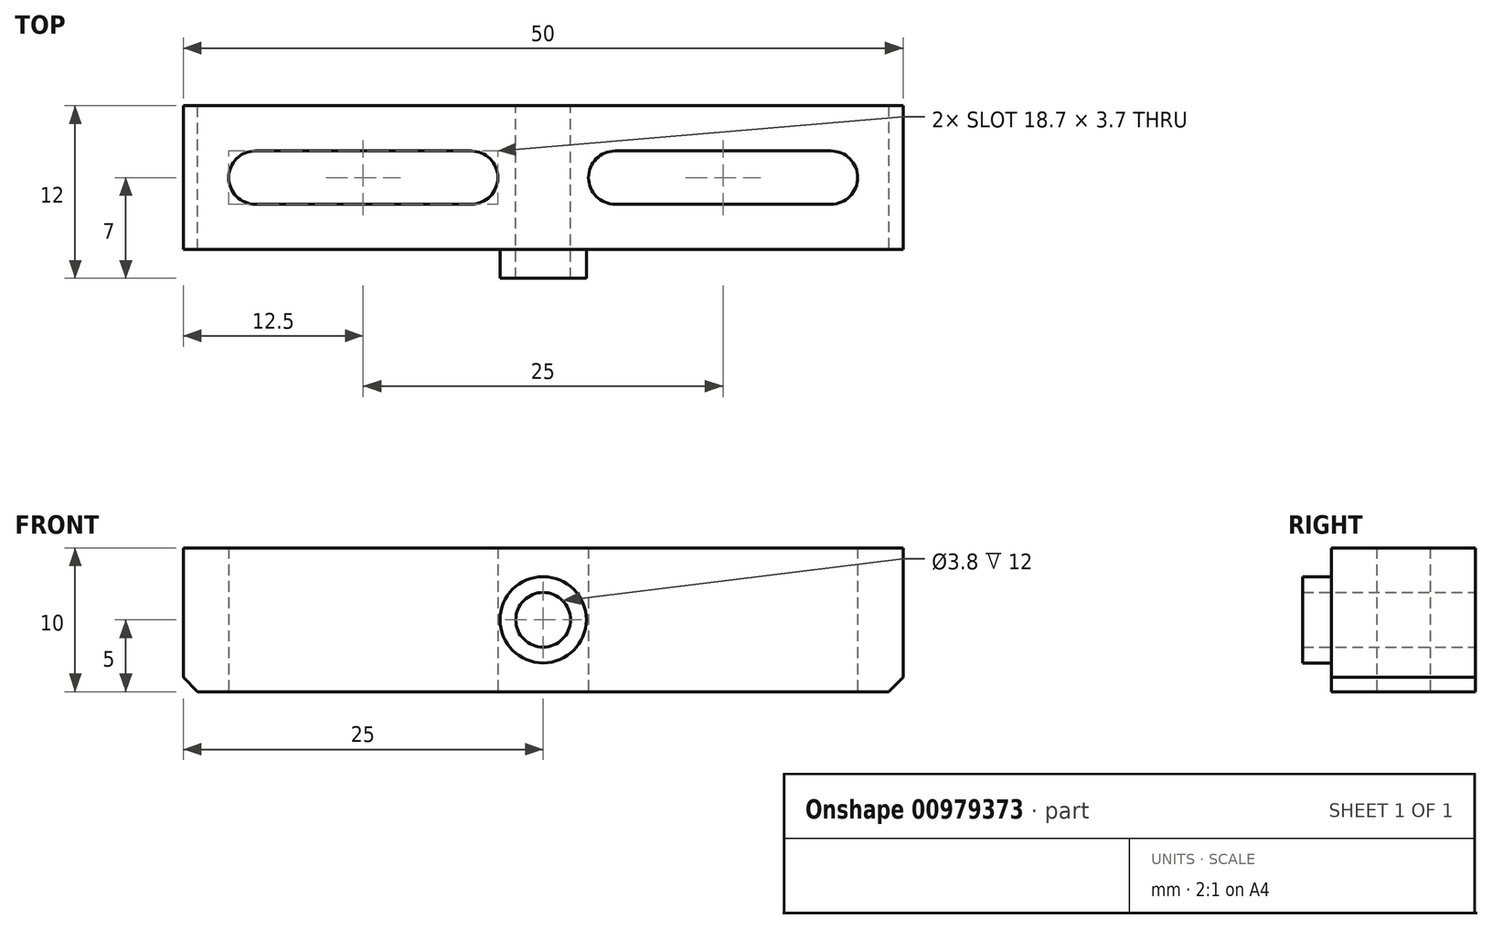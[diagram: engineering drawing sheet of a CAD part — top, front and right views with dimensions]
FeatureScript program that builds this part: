
annotation { "Feature Type Name" : "Feature", "Feature Type Description" : "" }
export const myFeature = defineFeature(function(context is Context, id is Id, definition is map)
    precondition{}
    {
        {
            var Q0;
            Q0=qCreatedBy(makeId("Front.planeOp"),FACE);
            var sketch = newSketch(context, id + "F0", { "sketchPlane" : qUnion([Q0])});
            skLineSegment(sketch, "E0.bottom", {"start": v(-25, 5) * mm, "end": v(25, 5) * mm});
            skLineSegment(sketch, "E0.top", {"start": v(-25, -5) * mm, "end": v(25, -5) * mm});
            skLineSegment(sketch, "E0.left", {"start": v(-25, 5) * mm, "end": v(-25, -5) * mm});
            skLineSegment(sketch, "E0.right", {"start": v(25, 5) * mm, "end": v(25, -5) * mm});
            skCircle(sketch, "E1", {"center": v(0, 0) * mm, "radius": 1.9 * mm});
            skSolve(sketch);
        }
        {
            var Q0;
            Q0=makeQuery(id+"F0.imprint","IMPRINT",FACE,{"disambiguationData":[TD([[makeQuery(id+"F0.imprint","IMPRINT",EDGE,{"derivedFrom":sQuery(id+"F0.wireOp",EDGE,"E0.top")}),1.0]])]});
            var Q1;
            Q1=makeQuery(id+"F0.imprint","IMPRINT",FACE,{"disambiguationData":[TD([[makeQuery(id+"F0.imprint","IMPRINT",EDGE,{"derivedFrom":sQuery(id+"F0.wireOp",EDGE,"WQmV3pCq-aRhs-lOnZ-NjPH-xWmHPh12bcor.bottom")}),-1.0]])]});
            var Q2;
            Q2=makeQuery(id+"F0.imprint","IMPRINT",FACE,{"disambiguationData":[TD([[makeQuery(id+"F0.imprint","IMPRINT",EDGE,{"derivedFrom":sQuery(id+"F0.wireOp",EDGE,"4fe1e560-5f00-40fb-89e2-31eaf53a3c980.MirrorCS")}),1.0]])]});
            var Q3;
            Q3=makeQuery(id+"F0.imprint","IMPRINT",FACE,{"disambiguationData":[TD([[makeQuery(id+"F0.imprint","IMPRINT",EDGE,{"derivedFrom":sQuery(id+"F0.wireOp",EDGE,"ZNvJAWPE-tP20-W4cz-rGWo-qfeXD5whcLuB")}),-1.0]])]});
            var Q4;
            Q4=makeQuery(id+"F0.imprint","IMPRINT",FACE,{"disambiguationData":[TD([[makeQuery(id+"F0.imprint","IMPRINT",EDGE,{"derivedFrom":sQuery(id+"F0.wireOp",EDGE,"E1")}),-1.0]])]});
            var Q5;
            Q5=makeQuery(id+"F0.imprint","IMPRINT",FACE,{"disambiguationData":[TD([[makeQuery(id+"F0.imprint","IMPRINT",EDGE,{"derivedFrom":sQuery(id+"F0.wireOp",EDGE,"fFYV0rMq-jki3-MS3X-DClv-uZveLAqEbOBl")}),1.0]])]});
            extrude(context, id + "F1", {"entities" : qUnion([Q0, Q1, Q2, Q3, Q4, Q5]), "endBound" : BoundingType.SYMMETRIC, "depth" : 10 * mm, "offsetDistance" : 25 * mm});
        }
        {
            var Q0;
            Q0=makeQuery(id+"F1.opExtrude","SWEPT_EDGE",EDGE,{"disambiguationData":[OSD([sQuery(id+"F0.wireOp",EDGE,"E0.top"),sQuery(id+"F0.wireOp",EDGE,"E0.left")])]});
            var Q1;
            Q1=makeQuery(id+"F1.opExtrude","SWEPT_EDGE",EDGE,{"disambiguationData":[OSD([sQuery(id+"F0.wireOp",EDGE,"E0.top"),sQuery(id+"F0.wireOp",EDGE,"E0.right")])]});
            chamfer(context, id + "F2", {"entities" : qUnion([Q0, Q1]), "width" : 1 * mm, "tangentPropagation" : true});
        }
        {
            var Q0;
            Q0=qCreatedBy(makeId("Top.planeOp"),FACE);
            var sketch = newSketch(context, id + "F3", { "sketchPlane" : qUnion([Q0])});
            skLineSegment(sketch, "E2", {"start": v(-20, 0) * mm, "end": v(-5, 0) * mm, "construction": true});
            skArc(sketch, "E3.0.startCap", {"start": v(-20, -1.85) * mm, "mid": v(-21.85, 0) * mm, "end": v(-20, 1.85) * mm});
            skArc(sketch, "E3.0.endCap", {"start": v(-5, 1.85) * mm, "mid": v(-3.15, 0) * mm, "end": v(-5, -1.85) * mm});
            skLineSegment(sketch, "E3.0.left", {"start": v(-20, 1.85) * mm, "end": v(-5, 1.85) * mm});
            skLineSegment(sketch, "E3.0.right", {"start": v(-20, -1.85) * mm, "end": v(-5, -1.85) * mm});
            skArc(sketch, "E4.MirrorCS", {"start": v(20, -1.85) * mm, "mid": v(21.85, 0) * mm, "end": v(20, 1.85) * mm});
            skLineSegment(sketch, "E5.MirrorCS", {"start": v(20, 0) * mm, "end": v(5, 0) * mm, "construction": true});
            skLineSegment(sketch, "E6.MirrorCS", {"start": v(20, 1.85) * mm, "end": v(5, 1.85) * mm});
            skLineSegment(sketch, "E7.MirrorCS", {"start": v(20, -1.85) * mm, "end": v(5, -1.85) * mm});
            skArc(sketch, "E8.MirrorCS", {"start": v(5, 1.85) * mm, "mid": v(3.15, 0) * mm, "end": v(5, -1.85) * mm});
            skSolve(sketch);
        }
        {
            var Q0;
            Q0 = qSketchRegion(id + "F3", true);
            extrude(context, id + "F4", {"entities" : qUnion([Q0]), "operationType" : NewBodyOperationType.REMOVE, "endBound" : BoundingType.SYMMETRIC, "depth" : 25 * mm, "offsetDistance" : 25 * mm});
        }
        {
            var Q0;
            Q0=makeQuery(id+"F1.opExtrude","CAP_FACE",FACE,{"disambiguationData":[OSD([sQuery(id+"F0.wireOp",EDGE,"E0.bottom"),sQuery(id+"F0.wireOp",EDGE,"E0.top"),sQuery(id+"F0.wireOp",EDGE,"E0.left"),sQuery(id+"F0.wireOp",EDGE,"E0.right"),sQuery(id+"F0.wireOp",EDGE,"E1")])],"isStart":false});
            var sketch = newSketch(context, id + "F5", { "sketchPlane" : qUnion([Q0])});
            skCircle(sketch, "E9", {"center": v(0, 0) * mm, "radius": 3 * mm});
            skSolve(sketch);
        }
        {
            var Q0;
            Q0=makeQuery(id+"F5.imprint","IMPRINT",FACE,{"disambiguationData":[TD([[makeQuery(id+"F5.imprint","IMPRINT",EDGE,{"derivedFrom":sQuery(id+"F5.wireOp",EDGE,"E9")}),1.0]])]});
            extrude(context, id + "F6", {"entities" : qUnion([Q0]), "operationType" : NewBodyOperationType.ADD, "depth" : 2 * mm, "offsetDistance" : 25 * mm});
        }
    });
